# Revit family: Petal_CB-292M_BIM
name_source: partatom
category: Arredi
units: mm (PartAtom-declared; Revit-internal decimal feet)

## family parameters
Attiva taglio nelle viste = No
Basato su piano di lavoro = No
Condiviso = No
Numero OmniClass = 23.40.20.00
Origine composizione di rendering = Geometria famiglia
Punto di calcolo locali = No
Sempre verticale = Sì
Taglio con vuoti quando caricato = No
Titolo OmniClass = General Furniture and Specialties

## types (1)
- CB-292M
    AVAILABLE FINISHES = Ebonized black lacquer on Oak (EB). Raw effect lacquer on Oak (RE). Natural lacquer on Oak or Walnut (NC). Base: smoke powder coat finish (SP).
    BASE MATERIAL = BASSAM_FELLOWS_OAK_O-NA
    BIM BADGE = https://bim.archiproducts.com
    COLLECTION = Petal
    DEPTH = 500 mm
    Descrizione = Wood and steel bar stool with back
    HEIGHT = 876 mm
    MATERIAL DESCRIPTION = Tubular steel base. 3D veneer plywood shell. Solid rod steel footrest.
    Modello = Petal Counter Stool Metal Base
    PRODUCT CODE = CB-292M
    PRODUCT SHEET = https://www.archiproducts.com
    Produttore = BassamFellows
    Prospetto di default = 0 mm  [stored 0 ft]
    STRUCTURE MATERIAL = BASSAM_FELLOWS_BRONZE_BZ
    TECHNICAL SHEET = https://www.archiproducts.com
    UPHOLSTERY MATERIAL = BASSAM_FELLOWS_COMFORT_LEATHER_43632_CAMEL
    URL = https://bassamfellows.com
    WIDTH = 434 mm

note: [stored X ft] marks values corroborated as IEEE doubles in the binary element streams (Revit-internal decimal feet)

## geometry (parser evidence)
native form markers: Sweep x3
no freeform markers — native parametric forms only
